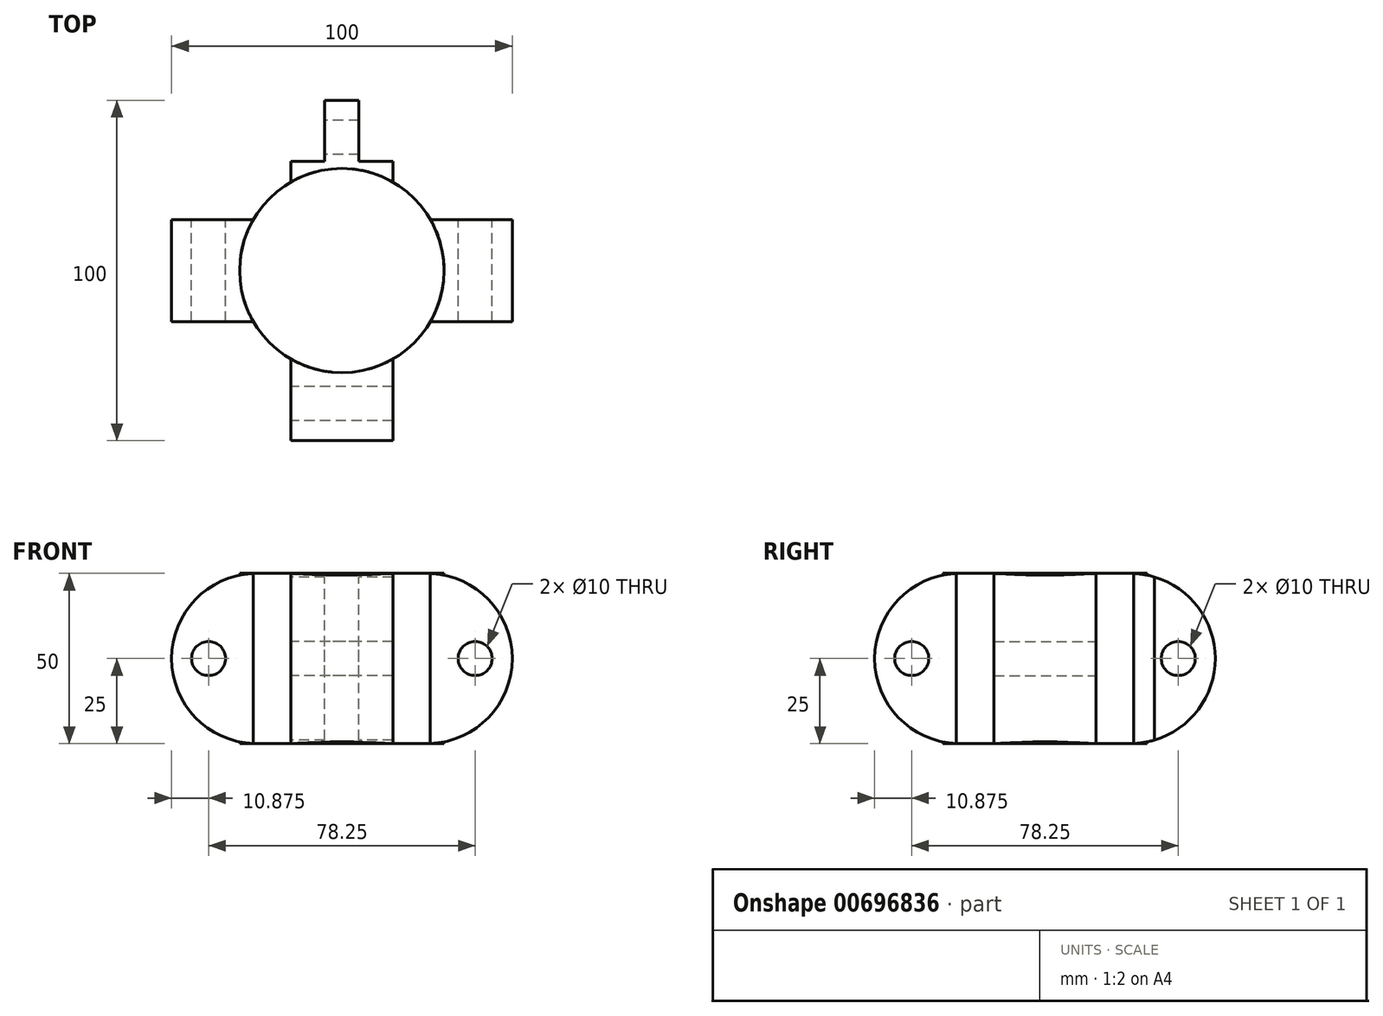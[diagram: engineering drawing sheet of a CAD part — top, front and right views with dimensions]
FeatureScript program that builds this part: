
annotation { "Feature Type Name" : "Feature", "Feature Type Description" : "" }
export const myFeature = defineFeature(function(context is Context, id is Id, definition is map)
    precondition{}
    {
        {
            var Q0;
            Q0=qCreatedBy(makeId("Front.planeOp"),FACE);
            var sketch = newSketch(context, id + "F0", { "sketchPlane" : qUnion([Q0])});
            skLineSegment(sketch, "E0.bottom", {"start": v(0, 0) * mm, "end": v(-25, 0) * mm});
            skLineSegment(sketch, "E0.top", {"start": v(0, 50) * mm, "end": v(-25, 50) * mm});
            skLineSegment(sketch, "E0.left", {"start": v(0, 0) * mm, "end": v(0, 50) * mm});
            skLineSegment(sketch, "E0.right", {"start": v(-25, 0) * mm, "end": v(-25, 50) * mm});
            skArc(sketch, "E1", {"start": v(-25, 50) * mm, "mid": v(-50, 25) * mm, "end": v(-25, 0) * mm});
            skCircle(sketch, "E2", {"center": v(-39.12, 25) * mm, "radius": 5 * mm});
            skLineSegment(sketch, "E3", {"start": v(0, -43.63) * mm, "end": v(0, 64.87) * mm, "construction": true});
            skArc(sketch, "E4.MirrorCS", {"start": v(25, 50) * mm, "mid": v(50, 25) * mm, "end": v(25, 0) * mm});
            skCircle(sketch, "E5.MirrorC", {"center": v(39.12, 25) * mm, "radius": 5 * mm});
            skLineSegment(sketch, "E6.MirrorCS", {"start": v(25, 0) * mm, "end": v(25, 50) * mm});
            skLineSegment(sketch, "E7.MirrorCS", {"start": v(0, 50) * mm, "end": v(25, 50) * mm});
            skLineSegment(sketch, "E8.MirrorCS", {"start": v(0, 0) * mm, "end": v(25, 0) * mm});
            skSolve(sketch);
        }
        {
            var Q0;
            Q0=qSketchRegion(id+"F0",true);
            extrude(context, id + "F1", {"entities" : qUnion([Q0]), "depth" : 15 * mm, "offsetDistance" : 25 * mm, "hasSecondDirection" : true, "secondDirectionOppositeDirection" : true, "secondDirectionDepth" : 15 * mm});
        }
        {
            var Q0;
            Q0=makeQuery(id+"F1.opExtrude","SWEPT_BODY",BODY,{"disambiguationData":[OSD([sQuery(id+"F0.wireOp",EDGE,"E0.bottom"),sQuery(id+"F0.wireOp",EDGE,"E0.top"),sQuery(id+"F0.wireOp",EDGE,"E1"),sQuery(id+"F0.wireOp",EDGE,"E2"),sQuery(id+"F0.wireOp",EDGE,"E4.MirrorCS"),sQuery(id+"F0.wireOp",EDGE,"E5.MirrorC"),sQuery(id+"F0.wireOp",EDGE,"E7.MirrorCS"),sQuery(id+"F0.wireOp",EDGE,"E8.MirrorCS")])]});
            var Q1;
            Q1=sQuery(id+"F0.wireOp",EDGE,"E3");
            circularPattern(context, id + "F2", {"operationType" : NewBodyOperationType.ADD, "entities" : qUnion([Q0]), "axis" : qUnion([Q1]), "angle" : 90 * degree, "instanceCount" : 2, "equalSpace" : true});
        }
        {
            var Q0;
            Q0=makeQuery(id+"F2.opPattern","COPY",FACE,{"derivedFrom":makeQuery(id+"F1.opExtrude","SWEPT_FACE",FACE,{"disambiguationData":[OSD([sQuery(id+"F0.wireOp",EDGE,"E0.top"),sQuery(id+"F0.wireOp",EDGE,"E7.MirrorCS")])]}),"instanceName":"1"});
            var sketch = newSketch(context, id + "F3", { "sketchPlane" : qUnion([Q0])});
            skCircle(sketch, "E9", {"center": v(0, 0) * mm, "radius": 30 * mm});
            skSolve(sketch);
        }
        {
            var Q0;
            Q0=qSketchRegion(id+"F3",true);
            var Q1;
            Q1=makeQuery(id+"F2.opPattern","COPY",FACE,{"derivedFrom":makeQuery(id+"F1.opExtrude","SWEPT_FACE",FACE,{"disambiguationData":[OSD([sQuery(id+"F0.wireOp",EDGE,"E0.bottom"),sQuery(id+"F0.wireOp",EDGE,"E8.MirrorCS")])]}),"instanceName":"1"});
            extrude(context, id + "F4", {"entities" : qUnion([Q0]), "operationType" : NewBodyOperationType.ADD, "endBound" : BoundingType.UP_TO_SURFACE, "oppositeDirection" : true, "depth" : 25 * mm, "endBoundEntityFace" : qUnion([Q1]), "offsetDistance" : 25 * mm});
        }
        {
            var Q0;
            {var subQ0=makeQuery(id+"F1.opExtrude","SWEPT_FACE",FACE,{"disambiguationData":[OSD([sQuery(id+"F0.wireOp",EDGE,"E0.top"),sQuery(id+"F0.wireOp",EDGE,"E7.MirrorCS")])]});Q0=makeQuery(id+"F4.boolean.opBoolean","MERGE",FACE,{"derivedFrom":[makeQuery(id+"F2.boolean.opBoolean","MERGE",FACE,{"derivedFrom":[subQ0,makeQuery(id+"F2.opPattern","COPY",FACE,{"derivedFrom":subQ0,"instanceName":"1"})]}),makeQuery(id+"F4.opExtrude","CAP_FACE",FACE,{"disambiguationData":[OSD([sQuery(id+"F3.wireOp",EDGE,"E9")])],"isStart":true})]});}
            var sketch = newSketch(context, id + "F5", { "sketchPlane" : qUnion([Q0])});
            skLineSegment(sketch, "E10.bottom", {"start": v(5, 32.12) * mm, "end": v(-5, 32.12) * mm});
            skLineSegment(sketch, "E10.top", {"start": v(5, 96.13) * mm, "end": v(-5, 96.13) * mm});
            skLineSegment(sketch, "E10.left", {"start": v(5, 32.12) * mm, "end": v(5, 96.13) * mm});
            skLineSegment(sketch, "E10.right", {"start": v(-5, 32.12) * mm, "end": v(-5, 96.13) * mm});
            skPoint(sketch, "E10.middle", {"position": v(0, 64.13) * mm});
            skLineSegment(sketch, "E11.bottom", {"start": v(0, 32.12) * mm, "end": v(0, 32.12) * mm});
            skLineSegment(sketch, "E11.top", {"start": v(0, 32.12) * mm, "end": v(0, 32.12) * mm});
            skLineSegment(sketch, "E11.left", {"start": v(0, 32.12) * mm, "end": v(0, 32.12) * mm});
            skLineSegment(sketch, "E11.right", {"start": v(0, 32.12) * mm, "end": v(0, 32.12) * mm});
            skPoint(sketch, "E11.middle", {"position": v(0, 32.12) * mm});
            skPoint(sketch, "E11.cornerSnap0", {"position": v(0, 32.12) * mm});
            skLineSegment(sketch, "E12.bottom", {"start": v(5, 32.12) * mm, "end": v(37.09, 32.12) * mm});
            skLineSegment(sketch, "E12.top", {"start": v(5, 75.54) * mm, "end": v(37.09, 75.54) * mm});
            skLineSegment(sketch, "E12.left", {"start": v(5, 32.12) * mm, "end": v(5, 75.54) * mm});
            skLineSegment(sketch, "E12.right", {"start": v(37.09, 32.12) * mm, "end": v(37.09, 75.54) * mm});
            skLineSegment(sketch, "E13.bottom", {"start": v(-5, 32.12) * mm, "end": v(-41.17, 32.12) * mm});
            skLineSegment(sketch, "E13.top", {"start": v(-5, 66.95) * mm, "end": v(-41.17, 66.95) * mm});
            skLineSegment(sketch, "E13.left", {"start": v(-5, 32.12) * mm, "end": v(-5, 66.95) * mm});
            skLineSegment(sketch, "E13.right", {"start": v(-41.17, 32.12) * mm, "end": v(-41.17, 66.95) * mm});
            skSolve(sketch);
        }
        {
            var Q0;
            Q0=makeQuery(id+"F5.imprint","IMPRINT",FACE,{"disambiguationData":[TD([[makeQuery(id+"F5.imprint","IMPRINT",EDGE,{"derivedFrom":sQuery(id+"F5.wireOp",EDGE,"E13.bottom")}),-1.0]])]});
            var Q1;
            Q1=makeQuery(id+"F5.imprint","IMPRINT",FACE,{"disambiguationData":[TD([[makeQuery(id+"F5.imprint","IMPRINT",EDGE,{"derivedFrom":sQuery(id+"F5.wireOp",EDGE,"E12.bottom")}),1.0]])]});
            extrude(context, id + "F6", {"entities" : qUnion([Q0, Q1]), "operationType" : NewBodyOperationType.REMOVE, "endBound" : BoundingType.THROUGH_ALL, "oppositeDirection" : true, "depth" : 25 * mm, "offsetDistance" : 25 * mm});
        }
    });
